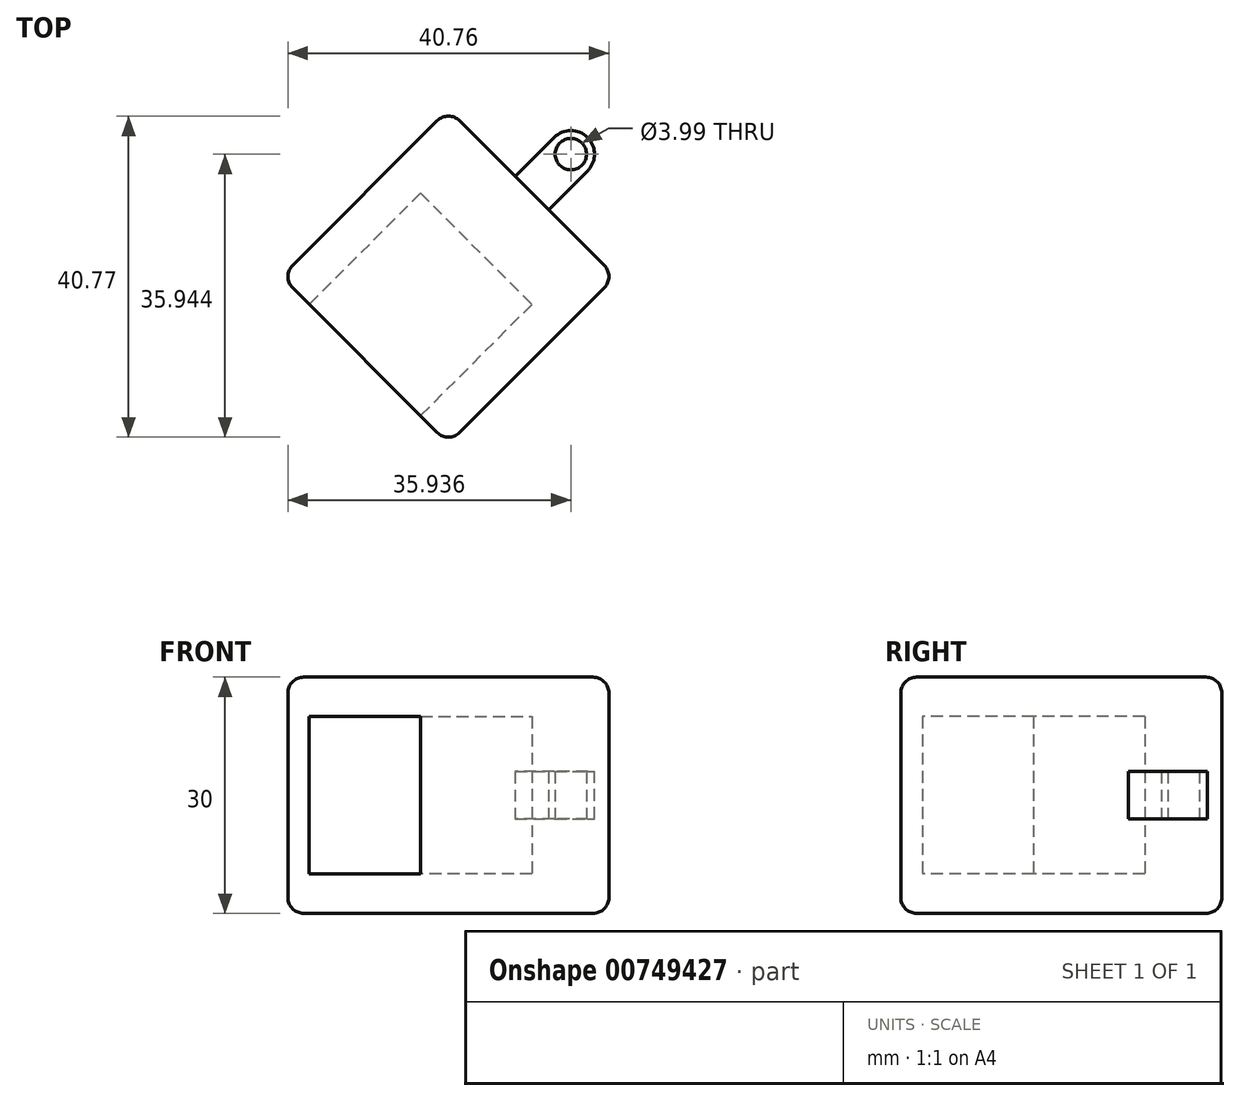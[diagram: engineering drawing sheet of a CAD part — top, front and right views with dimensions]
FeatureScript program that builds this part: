
annotation { "Feature Type Name" : "Feature", "Feature Type Description" : "" }
export const myFeature = defineFeature(function(context is Context, id is Id, definition is map)
    precondition{}
    {
        {
            var Q0;
            Q0=qCreatedBy(makeId("Top.planeOp"),FACE);
            var sketch = newSketch(context, id + "F0", { "sketchPlane" : qUnion([Q0])});
            skLineSegment(sketch, "E0", {"start": v(0, 0) * mm, "end": v(-21.21, 21.21) * mm});
            skLineSegment(sketch, "E1", {"start": v(-21.21, 21.21) * mm, "end": v(0, 42.43) * mm});
            skLineSegment(sketch, "E2", {"start": v(0, 42.43) * mm, "end": v(21.21, 21.21) * mm});
            skLineSegment(sketch, "E3", {"start": v(21.21, 21.21) * mm, "end": v(0, 0) * mm});
            skSolve(sketch);
        }
        {
            var Q0;
            Q0 = qSketchRegion(id + "F0", true);
            extrude(context, id + "F1", {"entities" : qUnion([Q0]), "depth" : 30 * mm, "offsetDistance" : 25.4 * mm});
        }
        {
            var Q0;
            Q0=makeQuery(id+"F1.opExtrude","SWEPT_FACE",FACE,{"disambiguationData":[OSD([sQuery(id+"F0.wireOp",EDGE,"E0")])]});
            var sketch = newSketch(context, id + "F2", { "sketchPlane" : qUnion([Q0])});
            skLineSegment(sketch, "E4.bottom", {"start": v(-25, 25) * mm, "end": v(-5, 25) * mm});
            skLineSegment(sketch, "E4.top", {"start": v(-25, 5) * mm, "end": v(-5, 5) * mm});
            skLineSegment(sketch, "E4.left", {"start": v(-25, 25) * mm, "end": v(-25, 5) * mm});
            skLineSegment(sketch, "E4.right", {"start": v(-5, 25) * mm, "end": v(-5, 5) * mm});
            skPoint(sketch, "E4.middle", {"position": v(-15, 15) * mm});
            skPoint(sketch, "E4.middle.positionSnap0", {"position": v(-15, 0) * mm});
            skPoint(sketch, "E4.centerSnap0", {"position": v(-15, 0) * mm});
            skSolve(sketch);
        }
        {
            var Q0;
            Q0 = qSketchRegion(id + "F2", true);
            extrude(context, id + "F3", {"entities" : qUnion([Q0]), "operationType" : NewBodyOperationType.REMOVE, "oppositeDirection" : true, "depth" : 20 * mm, "offsetDistance" : 25.4 * mm});
        }
        {
            var Q0;
            Q0=makeQuery(id+"F1.opExtrude","SWEPT_FACE",FACE,{"disambiguationData":[OSD([sQuery(id+"F0.wireOp",EDGE,"E1")])]});
            var Q1;
            Q1=makeQuery(id+"F1.opExtrude","CAP_FACE",FACE,{"disambiguationData":[OSD([sQuery(id+"F0.wireOp",EDGE,"E0"),sQuery(id+"F0.wireOp",EDGE,"E1"),sQuery(id+"F0.wireOp",EDGE,"E2"),sQuery(id+"F0.wireOp",EDGE,"E3")])],"isStart":false});
            var Q2;
            Q2=makeQuery(id+"F1.opExtrude","SWEPT_FACE",FACE,{"disambiguationData":[OSD([sQuery(id+"F0.wireOp",EDGE,"E3")])]});
            var Q3;
            Q3=makeQuery(id+"F1.opExtrude","SWEPT_FACE",FACE,{"disambiguationData":[OSD([sQuery(id+"F0.wireOp",EDGE,"E2")])]});
            var Q4;
            Q4=makeQuery(id+"F1.opExtrude","CAP_FACE",FACE,{"disambiguationData":[OSD([sQuery(id+"F0.wireOp",EDGE,"E0"),sQuery(id+"F0.wireOp",EDGE,"E1"),sQuery(id+"F0.wireOp",EDGE,"E2"),sQuery(id+"F0.wireOp",EDGE,"E3")])],"isStart":true});
            var Q5;
            Q5=makeQuery(id+"F1.opExtrude","SWEPT_EDGE",EDGE,{"disambiguationData":[OSD([sQuery(id+"F0.wireOp",EDGE,"E0"),sQuery(id+"F0.wireOp",EDGE,"E3")])]});
            fillet(context, id + "F4", {"entities" : qUnion([Q0, Q1, Q2, Q3, Q4, Q5]), "radius" : 2 * mm, "tangentPropagation" : true, "allowEdgeOverflow" : false});
        }
        {
            var Q0;
            Q0=makeQuery(id+"F1.opExtrude","SWEPT_FACE",FACE,{"disambiguationData":[OSD([sQuery(id+"F0.wireOp",EDGE,"E2")])]});
            var sketch = newSketch(context, id + "F5", { "sketchPlane" : qUnion([Q0])});
            skLineSegment(sketch, "E5.bottom", {"start": v(18, 18) * mm, "end": v(12, 18) * mm});
            skLineSegment(sketch, "E5.top", {"start": v(18, 12) * mm, "end": v(12, 12) * mm});
            skLineSegment(sketch, "E5.left", {"start": v(18, 18) * mm, "end": v(18, 12) * mm});
            skLineSegment(sketch, "E5.right", {"start": v(12, 18) * mm, "end": v(12, 12) * mm});
            skPoint(sketch, "E5.middle", {"position": v(15, 15) * mm});
            skSolve(sketch);
        }
        {
            var Q0;
            Q0 = qSketchRegion(id + "F5", true);
            extrude(context, id + "F6", {"entities" : qUnion([Q0]), "operationType" : NewBodyOperationType.ADD, "depth" : 10 * mm, "offsetDistance" : 25.4 * mm});
        }
        {
            var Q0;
            Q0=makeQuery(id+"F6.opExtrude","CAP_EDGE",EDGE,{"disambiguationData":[OSD([sQuery(id+"F5.wireOp",EDGE,"E5.right")])],"isStart":false});
            var Q1;
            Q1=makeQuery(id+"F6.opExtrude","CAP_EDGE",EDGE,{"disambiguationData":[OSD([sQuery(id+"F5.wireOp",EDGE,"E5.left")])],"isStart":false});
            fillet(context, id + "F7", {"entities" : qUnion([Q0, Q1]), "radius" : 3 * mm, "tangentPropagation" : true, "allowEdgeOverflow" : false});
        }
        {
            var Q0;
            Q0=makeQuery(id+"F6.opExtrude","SWEPT_FACE",FACE,{"disambiguationData":[OSD([sQuery(id+"F5.wireOp",EDGE,"E5.top")])]});
            var sketch = newSketch(context, id + "F8", { "sketchPlane" : qUnion([Q0])});
            skCircle(sketch, "E6", {"center": v(15.56, -36.77) * mm, "radius": 2 * mm});
            skSolve(sketch);
        }
        {
            var Q0;
            Q0 = qSketchRegion(id + "F8", true);
            extrude(context, id + "F9", {"entities" : qUnion([Q0]), "operationType" : NewBodyOperationType.REMOVE, "oppositeDirection" : true, "depth" : 6 * mm, "offsetDistance" : 25.4 * mm});
        }
    });
